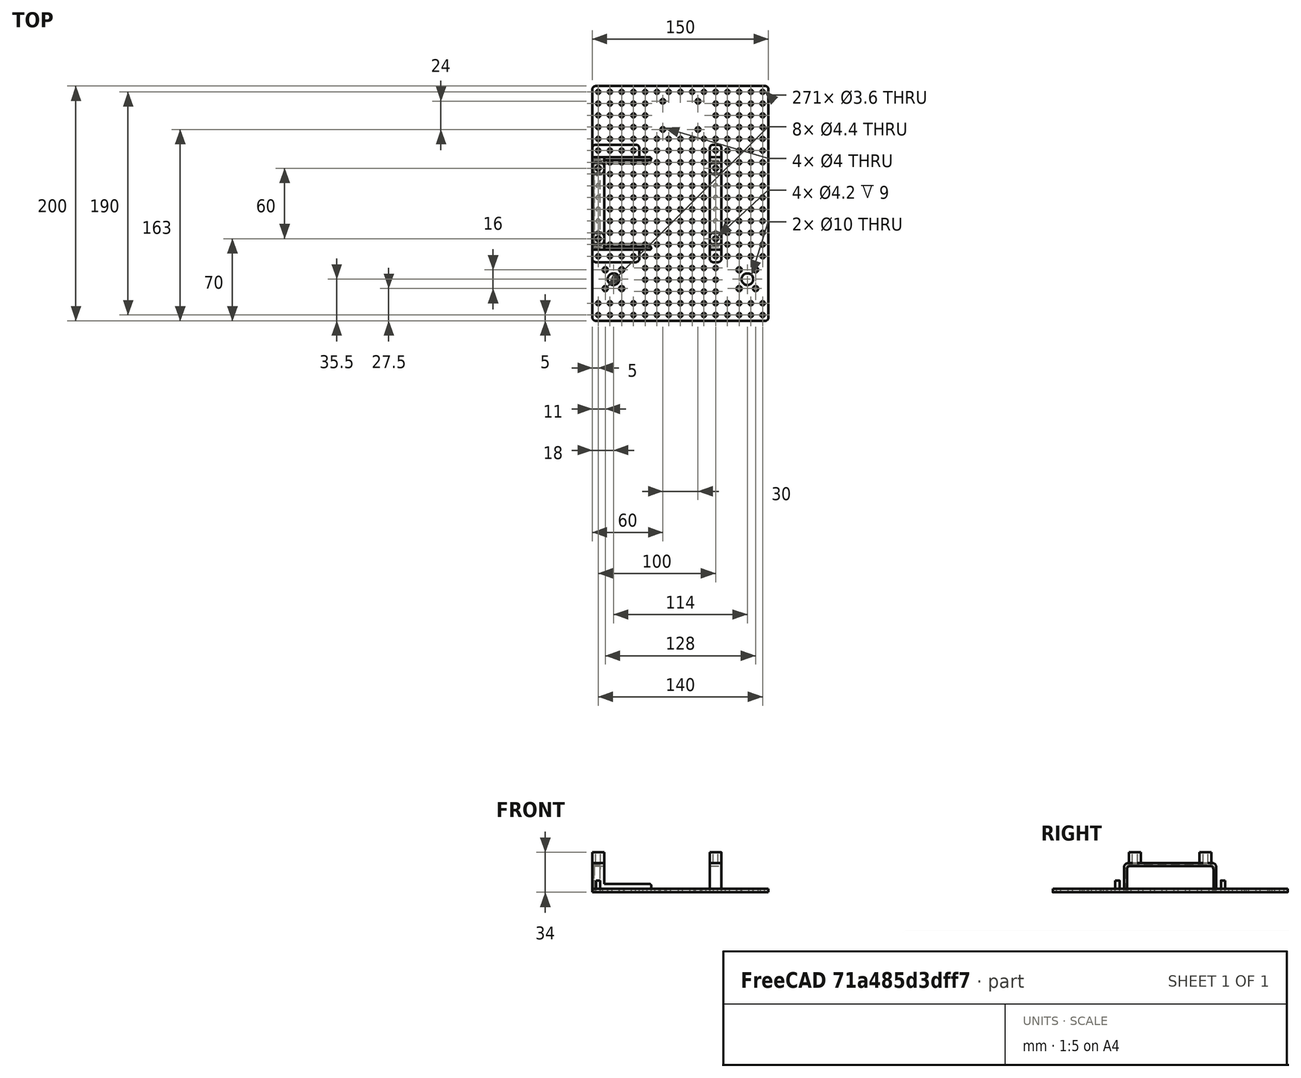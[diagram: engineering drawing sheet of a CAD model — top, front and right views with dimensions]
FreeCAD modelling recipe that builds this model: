
FCSTD DOCUMENT  (FreeCAD 0.19R23578 (Git))
Label: battery_holder
License: All rights reserved
LicenseURL: http://en.wikipedia.org/wiki/All_rights_reserved
objects: Part::Box×8, Part::Fillet×8, Part::Cut×7, Part::MultiFuse×4, Part::Cylinder×3, Part::Mirroring×3, Part::FeaturePython×1, Part::Feature×1
note: 34 computed .brp shape members not serialized (recipe doc carries the construction recipe); baked Part::Feature solids carry a one-line shape summary decoded from their .brp

FEATURE [Part::Box] Box  label="xiaomi battery"
  AttacherType = Attacher::AttachEngine3D
  Height = 22.5
  Length = 141
  Placement = pos=(2,0,0) rot=(0,0,1;0rad)
  Width = 73.6
FEATURE [Part::Fillet] Fillet  label="battery fillet"
  Base = -> Box
  Edges = 4 edges r=3: [Edge9,Edge10,Edge11,Edge12]
  Placement = pos=(0,-36.8,0) rot=(0,0,1;0rad)
  expr: .Placement.Base.y = -<<xiaomi battery>>.Width / 2
FEATURE [Part::Box] Box001  label="back wall"
  AttacherType = Attacher::AttachEngine3D
  Height = 25
  Length = 10
  Placement = pos=(0,-39.3,0) rot=(0,0,1;0rad)
  Width = 78.6
  expr: Height = <<xiaomi battery>>.Height + 2.5mm
  expr: Width = <<xiaomi battery>>.Width + 5mm
  expr: .Placement.Base.y = -Width / 2
FEATURE [Part::Box] Box002  label="back wall bottom"
  AttacherType = Attacher::AttachEngine3D
  Height = 3
  Length = 40
  Placement = pos=(0,-50,0) rot=(0,0,1;0rad)
  Width = 100
  expr: .Placement.Base.y = -Width / 2
  expr: Width = (round(<<back wall>>.Width / 10mm) + 2) * 10mm
FEATURE [Part::Fillet] Fillet001  label="back wall bottom fillet"
  Base = -> Box002
  Edges = 4 edges r=3: [Edge1,Edge3,Edge5,Edge7]
FEATURE [Part::Cylinder] Cylinder  label="bolt hole"
  Angle = 360
  AttacherType = Attacher::AttachEngine3D
  Height = 10
  Placement = pos=(5,45,0) rot=(0,0,1;0rad)
  Radius = 1.8
  expr: .Placement.Base.x = 5mm
  expr: .Placement.Base.y = <<back wall bottom>>.Width / 2 - 5mm
FEATURE [Part::Mirroring] Part__Mirroring  label="bolt hole (Mirror #1)"
  Base = (0,0,0)
  Normal = (0,1,0)
  Source = -> Cylinder
FEATURE [Part::Fillet] Fillet002  label="back wall fillet"
  Base = -> Box001
  Edges = 2 edges r=4: [Edge10,Edge12]
FEATURE [Part::Box] Box003  label="top insert box"
  AttacherType = Attacher::AttachEngine3D
  Height = 9
  Length = 10
  Placement = pos=(0,-5,0) rot=(0,0,1;0rad)
  Width = 10
  expr: .Placement.Base.y = -Width / 2
FEATURE [Part::Fillet] Fillet003  label="top insert box fillet"
  Base = -> Box003
  Edges = 4 edges r=3: [Edge1,Edge3,Edge5,Edge7]
FEATURE [Part::Cylinder] Cylinder001  label="insert hole"
  Angle = 360
  AttacherType = Attacher::AttachEngine3D
  Height = 10
  Placement = pos=(5,0,0) rot=(0,0,1;0rad)
  Radius = 2.1
  expr: .Placement.Base.x = <<top insert box>>.Length / 2
FEATURE [Part::Cut] Cut  label="top insert box cut"
  Base = -> Fillet003
  Placement = pos=(0,30,25) rot=(0,0,1;0rad)
  Tool = -> Cylinder001
  expr: .Placement.Base.z = <<back wall>>.Height
  expr: .Placement.Base.y = (round(<<back wall>>.Width / 10mm) / 2 - 1) * 10mm
FEATURE [Part::Mirroring] Part__Mirroring001  label="top insert box cut (Mirror #2)"
  Base = (0,0,0)
  Normal = (0,1,0)
  Source = -> Cut
FEATURE [Part::MultiFuse] Fusion  label="bolt hole fusion"
  Shapes = -> [Part__Mirroring,Cylinder]
FEATURE [Part::Box] Box004  label="test back wall"
  AttacherType = Attacher::AttachEngine3D
  Height = 23.5
  Length = 5
  Placement = pos=(1.5,-37.8,0) rot=(0,0,1;0rad)
  Width = 75.6
  expr: .Placement.Base.y = -Width / 2
  expr: Width = <<xiaomi battery>>.Width + 2mm
  expr: Height = <<xiaomi battery>>.Height + 1mm
FEATURE [Part::Fillet] Fillet004  label="test back wall fillet"
  Base = -> Box004
  Edges = 2 edges r=4: [Edge10,Edge12]
FEATURE [Part::Cut] Cut003  label="test back wall cut"
  Base = -> Fillet004
  Tool = -> Fillet
FEATURE [Part::Box] Box005  label="big bottom cube"
  AttacherType = Attacher::AttachEngine3D
  Height = 7
  Length = 50
  Placement = pos=(0,-39.3,0) rot=(0,0,1;0rad)
  Width = 78.6
  expr: Width = <<back wall>>.Width
  expr: .Placement.Base.y = -Width / 2
FEATURE [Part::Cut] Cut004  label="big bottom cube cut"
  Base = -> Box005
  Tool = -> Fillet
FEATURE [Part::Fillet] Fillet005  label="big bottom cube fillet"
  Base = -> Cut004
  Edges = 8 edges r=1: [Edge6,Edge9,Edge13,Edge15,Edge21,Edge22,Edge23,Edge24]
FEATURE [Part::FeaturePython] Array  label="bolt hole array"  # Draft array (typed FeaturePython)
  Angle = 360
  ArrayType = 0
  Axis = (0,0,1)
  Base = -> Fusion
  Center = (0,0,0)
  Count = 4
  ExpandArray = false
  Fuse = false
  IntervalAxis = (0,0,0)
  IntervalX = (10,0,0)
  IntervalY = (0,100,0)
  IntervalZ = (0,0,100)
  NumberCircles = 3
  NumberPolar = 5
  NumberX = 4
  NumberY = 1
  NumberZ = 1
  PlacementList = 4 placements: arithmetic series from (0,0,0) step (10,0,0) to (30,0,0)
  RadialDistance = 50
  ScaleList = (4) [(1,1,1),(1,1,1),(1,1,1),(1,1,1)]
  Symmetry = 1
  TangentialDistance = 25
FEATURE [Part::Cut] Cut001  label="back wall bottom cut"
  Base = -> Fillet001
  Tool = -> Array
FEATURE [Part::MultiFuse] Fusion001  label="battery back wall fusion"
  Shapes = -> [Fillet002,Part__Mirroring001,Cut,Cut001,Fillet005]
FEATURE [Part::Cut] Cut002  label="battery back wall cut"
  Base = -> Fusion001
  Tool = -> Fillet
FEATURE [Part::Cylinder] Cylinder002  label="bolt hole001"
  Angle = 360
  AttacherType = Attacher::AttachEngine3D
  Height = 10
  Placement = pos=(5,45,0) rot=(0,0,1;0rad)
  Radius = 1.8
  expr: .Placement.Base.y = <<back wall bottom001>>.Width / 2 - 5mm
  expr: .Placement.Base.x = 5mm
FEATURE [Part::Box] Box006  label="back wall001"
  AttacherType = Attacher::AttachEngine3D
  Height = 25
  Length = 10
  Placement = pos=(0,-39.3,0) rot=(0,0,1;0rad)
  Width = 78.6
  expr: .Placement.Base.y = -Width / 2
  expr: Width = <<xiaomi battery>>.Width + 5mm
  expr: Height = <<xiaomi battery>>.Height + 2.5mm
FEATURE [Part::Box] Box007  label="back wall bottom001"
  AttacherType = Attacher::AttachEngine3D
  Height = 3
  Length = 10
  Placement = pos=(0,-50,0) rot=(0,0,1;0rad)
  Width = 100
  expr: Width = (round(<<back wall001>>.Width / 10mm) + 2) * 10mm
  expr: .Placement.Base.y = -Width / 2
FEATURE [Part::Fillet] Fillet006  label="back wall bottom fillet001"
  Base = -> Box007
  Edges = 4 edges r=3: [Edge1,Edge3,Edge5,Edge7]
FEATURE [Part::Mirroring] Part__Mirroring002  label="bolt hole (Mirror #1)001"
  Base = (0,0,0)
  Normal = (0,1,0)
  Source = -> Cylinder002
FEATURE [Part::MultiFuse] Fusion002  label="bolt hole fusion001"
  Shapes = -> [Part__Mirroring002,Cylinder002]
FEATURE [Part::Fillet] Fillet007  label="back wall fillet001"
  Base = -> Box006
  Edges = 2 edges r=4: [Edge10,Edge12]
FEATURE [Part::MultiFuse] Fusion003  label="battery frame fusion"
  Shapes = -> [Fillet006,Fillet007,Cut,Part__Mirroring001]
FEATURE [Part::Cut] Cut005  label="battery frame cut"
  Base = -> Fusion003
  Placement = pos=(100,0,0) rot=(0,0,1;0rad)
  Tool = -> Fusion002
FEATURE [Part::Cut] Cut006  label="battery frame"
  Base = -> Cut005
  Tool = -> Fillet
FEATURE [Part::Feature] Cut002001001  label="holed plate cut002"
  Placement = pos=(0,-78,0) rot=(0,0,1;0rad)
  shape: bbox 150 x 200 x 3 mm, 285 faces (baked)
